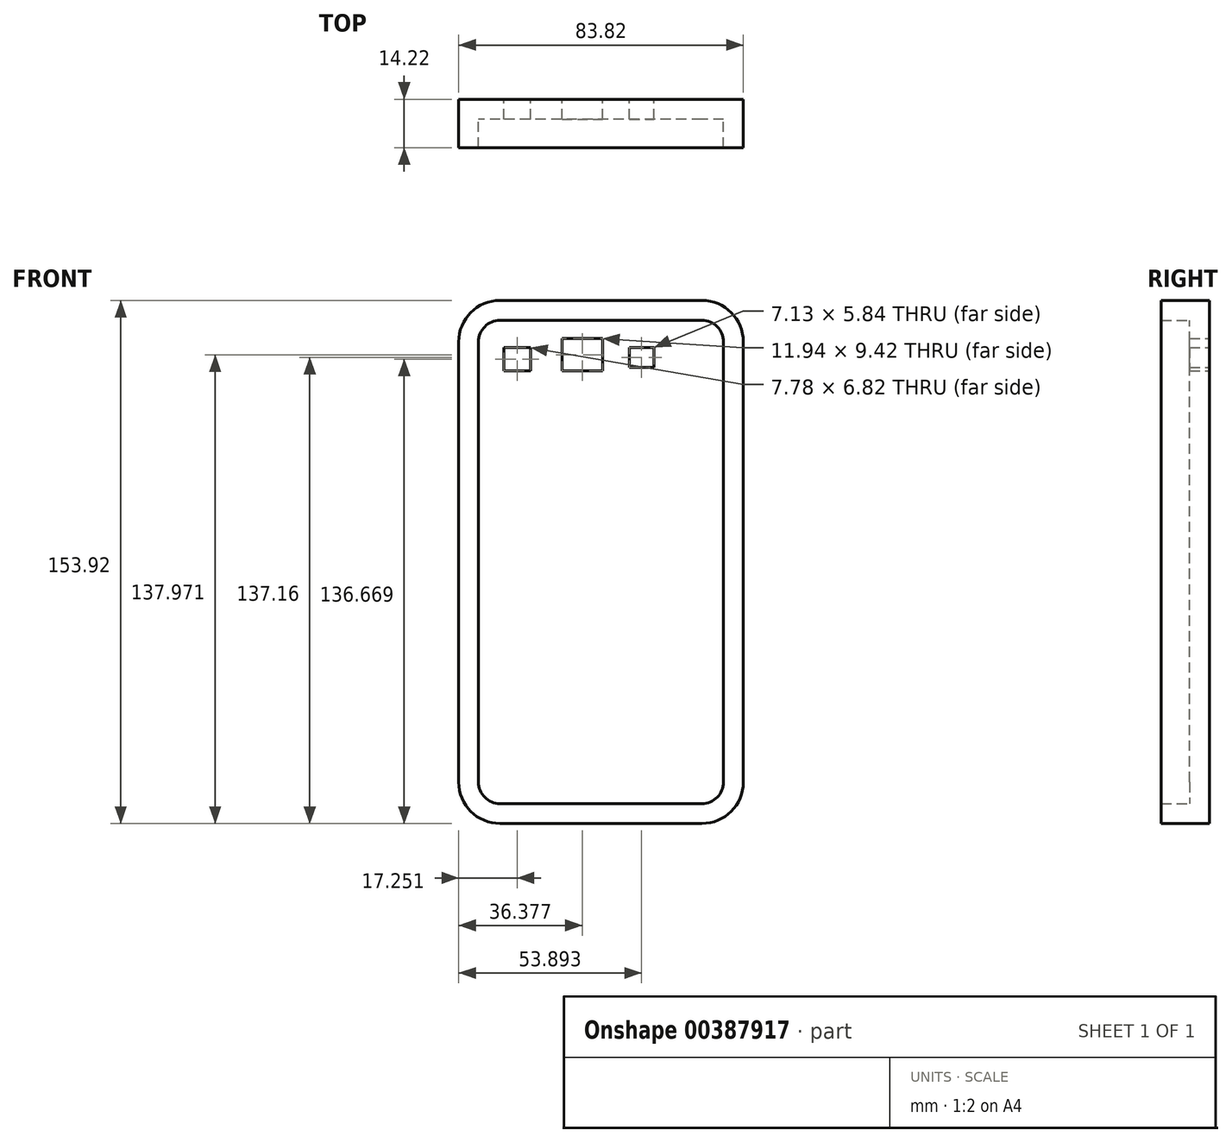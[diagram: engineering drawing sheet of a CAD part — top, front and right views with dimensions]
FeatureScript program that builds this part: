
annotation { "Feature Type Name" : "Feature", "Feature Type Description" : "" }
export const myFeature = defineFeature(function(context is Context, id is Id, definition is map)
    precondition{}
    {
        {
            var Q0;
            Q0=qCreatedBy(makeId("Front.planeOp"),FACE);
            var sketch = newSketch(context, id + "F0", { "sketchPlane" : qUnion([Q0])});
            skLineSegment(sketch, "E0.bottom", {"start": v(14.17, -64.62) * mm, "end": v(-45.26, -64.62) * mm});
            skLineSegment(sketch, "E0.top", {"start": v(14.17, 77.62) * mm, "end": v(-45.26, 77.62) * mm});
            skLineSegment(sketch, "E0.left", {"start": v(20.52, -58.27) * mm, "end": v(20.52, 71.27) * mm});
            skLineSegment(sketch, "E0.right", {"start": v(-51.61, -58.27) * mm, "end": v(-51.61, 71.27) * mm});
            skPoint(sketch, "E1.visualSharp", {"position": v(-51.61, 77.62) * mm});
            skArc(sketch, "E1.filletArc", {"start": v(-45.26, 77.62) * mm, "mid": v(-49.75, 75.76) * mm, "end": v(-51.61, 71.27) * mm});
            skPoint(sketch, "E2.visualSharp", {"position": v(20.52, 77.62) * mm});
            skArc(sketch, "E2.filletArc", {"start": v(20.52, 71.27) * mm, "mid": v(18.66, 75.76) * mm, "end": v(14.17, 77.62) * mm});
            skPoint(sketch, "E3.visualSharp", {"position": v(20.52, -64.62) * mm});
            skArc(sketch, "E3.filletArc", {"start": v(14.17, -64.62) * mm, "mid": v(18.66, -62.76) * mm, "end": v(20.52, -58.27) * mm});
            skPoint(sketch, "E4.visualSharp", {"position": v(-51.61, -64.62) * mm});
            skArc(sketch, "E4.filletArc", {"start": v(-51.61, -58.27) * mm, "mid": v(-49.75, -62.76) * mm, "end": v(-45.26, -64.62) * mm});
            skSolve(sketch);
        }
        {
            var Q0;
            Q0 = qSketchRegion(id + "F0", true);
            extrude(context, id + "F1", {"entities" : qUnion([Q0]), "depth" : 8.38 * mm});
        }
        {
            var Q0;
            Q0=makeQuery(id+"F1.opExtrude","CAP_FACE",FACE,{"disambiguationData":[OSD([sQuery(id+"F0.wireOp",EDGE,"E0.bottom"),sQuery(id+"F0.wireOp",EDGE,"E0.top"),sQuery(id+"F0.wireOp",EDGE,"E0.left"),sQuery(id+"F0.wireOp",EDGE,"E0.right"),sQuery(id+"F0.wireOp",EDGE,"E1.filletArc"),sQuery(id+"F0.wireOp",EDGE,"E2.filletArc"),sQuery(id+"F0.wireOp",EDGE,"E3.filletArc"),sQuery(id+"F0.wireOp",EDGE,"E4.filletArc")])],"isStart":false});
            shell(context, id + "F2", {"entities" : qUnion([Q0]), "thickness" : 5.84 * mm, "oppositeDirection" : true});
        }
        {
            var Q0;
            Q0=makeQuery(id+"F1.opExtrude","CAP_FACE",FACE,{"disambiguationData":[OSD([sQuery(id+"F0.wireOp",EDGE,"E0.bottom"),sQuery(id+"F0.wireOp",EDGE,"E0.top"),sQuery(id+"F0.wireOp",EDGE,"E0.left"),sQuery(id+"F0.wireOp",EDGE,"E0.right"),sQuery(id+"F0.wireOp",EDGE,"E1.filletArc"),sQuery(id+"F0.wireOp",EDGE,"E2.filletArc"),sQuery(id+"F0.wireOp",EDGE,"E3.filletArc"),sQuery(id+"F0.wireOp",EDGE,"E4.filletArc")])],"isStart":true});
            var sketch = newSketch(context, id + "F3", { "sketchPlane" : qUnion([Q0])});
            skLineSegment(sketch, "E5.bottom", {"start": v(27.05, 62.8) * mm, "end": v(15.11, 62.8) * mm});
            skLineSegment(sketch, "E5.top", {"start": v(27.05, 72.22) * mm, "end": v(15.11, 72.22) * mm});
            skLineSegment(sketch, "E5.left", {"start": v(27.05, 62.8) * mm, "end": v(27.05, 72.22) * mm});
            skLineSegment(sketch, "E5.right", {"start": v(15.11, 62.8) * mm, "end": v(15.11, 72.22) * mm});
            skLineSegment(sketch, "E6.bottom", {"start": v(7.13, 63.78) * mm, "end": v(0, 63.78) * mm});
            skLineSegment(sketch, "E6.top", {"start": v(7.13, 69.62) * mm, "end": v(0, 69.62) * mm});
            skLineSegment(sketch, "E6.left", {"start": v(7.13, 63.78) * mm, "end": v(7.13, 69.62) * mm});
            skLineSegment(sketch, "E6.right", {"start": v(0, 63.78) * mm, "end": v(0, 69.62) * mm});
            skPoint(sketch, "E7.oppositeSnap0", {"position": v(21.08, 62.8) * mm});
            skLineSegment(sketch, "E7.bottom", {"start": v(36.32, 69.62) * mm, "end": v(44.1, 69.62) * mm});
            skLineSegment(sketch, "E7.top", {"start": v(36.32, 62.8) * mm, "end": v(44.1, 62.8) * mm});
            skLineSegment(sketch, "E7.left", {"start": v(36.32, 69.62) * mm, "end": v(36.32, 62.8) * mm});
            skLineSegment(sketch, "E7.right", {"start": v(44.1, 69.62) * mm, "end": v(44.1, 62.8) * mm});
            skSolve(sketch);
        }
        {
            var Q0;
            Q0=makeQuery(id+"F3.imprint","IMPRINT",FACE,{"disambiguationData":[TD([[makeQuery(id+"F3.imprint","IMPRINT",EDGE,{"derivedFrom":sQuery(id+"F3.wireOp",EDGE,"E7.bottom")}),-1.0]])]});
            var Q1;
            Q1=makeQuery(id+"F3.imprint","IMPRINT",FACE,{"disambiguationData":[TD([[makeQuery(id+"F3.imprint","IMPRINT",EDGE,{"derivedFrom":sQuery(id+"F3.wireOp",EDGE,"E6.bottom")}),-1.0]])]});
            var Q2;
            Q2=makeQuery(id+"F3.imprint","IMPRINT",FACE,{"disambiguationData":[TD([[makeQuery(id+"F3.imprint","IMPRINT",EDGE,{"derivedFrom":sQuery(id+"F3.wireOp",EDGE,"E5.bottom")}),-1.0]])]});
            extrude(context, id + "F4", {"entities" : qUnion([Q0, Q1, Q2]), "operationType" : NewBodyOperationType.REMOVE, "oppositeDirection" : true, "depth" : 5.84 * mm});
        }
    });
